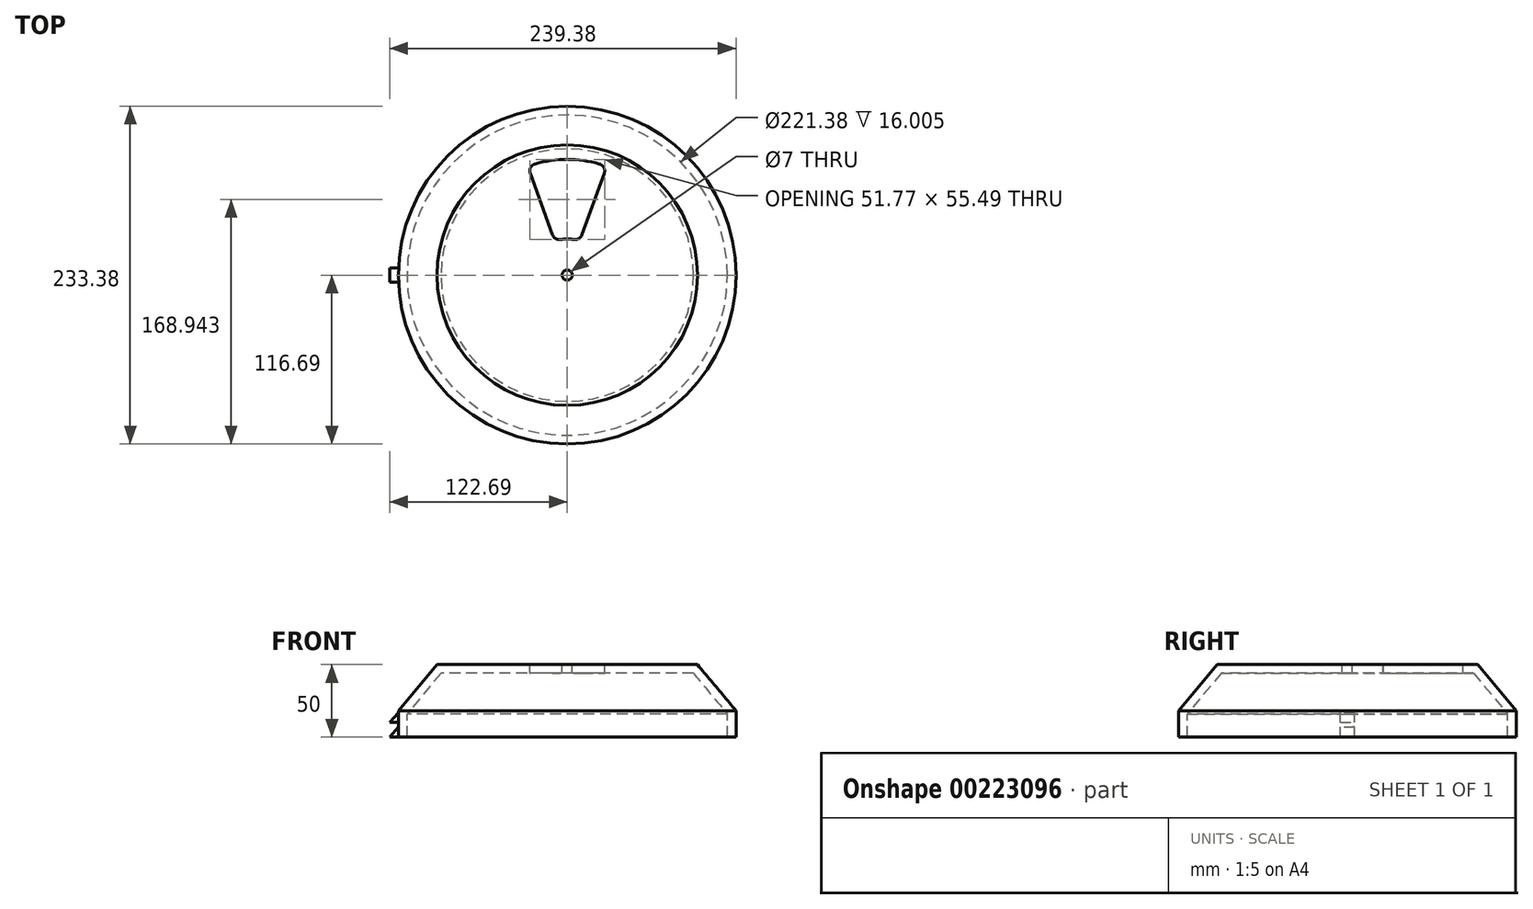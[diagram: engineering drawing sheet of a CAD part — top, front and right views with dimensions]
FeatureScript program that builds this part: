
annotation { "Feature Type Name" : "Feature", "Feature Type Description" : "" }
export const myFeature = defineFeature(function(context is Context, id is Id, definition is map)
    precondition{}
    {
        {
            var Q0;
            Q0=qCreatedBy(makeId("Front.planeOp"),FACE);
            var sketch = newSketch(context, id + "F0", { "sketchPlane" : qUnion([Q0])});
            skLineSegment(sketch, "E0", {"start": v(0, 0) * mm, "end": v(90, 0) * mm});
            skLineSegment(sketch, "E1", {"start": v(0, 0) * mm, "end": v(0, -6) * mm});
            skLineSegment(sketch, "E2", {"start": v(0, -6) * mm, "end": v(87.2, -6) * mm});
            skLineSegment(sketch, "E3", {"start": v(110.7, -34) * mm, "end": v(116.7, -31.81) * mm, "construction": true});
            skLineSegment(sketch, "E4", {"start": v(110.7, -34) * mm, "end": v(110.7, -50) * mm});
            skLineSegment(sketch, "E5", {"start": v(110.7, -50) * mm, "end": v(116.7, -50) * mm});
            skLineSegment(sketch, "E6", {"start": v(116.7, -50) * mm, "end": v(116.7, -31.81) * mm});
            skLineSegment(sketch, "E7", {"start": v(110.7, -34) * mm, "end": v(87.2, -6) * mm});
            skLineSegment(sketch, "E8", {"start": v(90, 0) * mm, "end": v(116.7, -31.81) * mm});
            skLineSegment(sketch, "E9", {"start": v(90, 0) * mm, "end": v(107.7, 0) * mm, "construction": true});
            skSolve(sketch);
        }
        {
            var Q0;
            Q0=makeQuery(id+"F0.imprint","IMPRINT",FACE,{"disambiguationData":[TD([[makeQuery(id+"F0.imprint","IMPRINT",EDGE,{"derivedFrom":sQuery(id+"F0.wireOp",EDGE,"E0")}),-1.0]])]});
            var Q1;
            Q1=sQuery(id+"F0.wireOp",EDGE,"E1");
            revolve(context, id + "F1", {"entities" : qUnion([Q0]), "axis" : qUnion([Q1]), "revolveType" : RevolveType.FULL});
        }
        {
            var Q0;
            Q0=makeQuery(id+"F1.opRevolve","SWEPT_FACE",FACE,{"disambiguationData":[OSD([sQuery(id+"F0.wireOp",EDGE,"E0")])]});
            var sketch = newSketch(context, id + "F2", { "sketchPlane" : qUnion([Q0])});
            skCircle(sketch, "E10", {"center": v(0, 0) * mm, "radius": 3.5 * mm});
            skSolve(sketch);
        }
        {
            var Q0;
            Q0 = qSketchRegion(id + "F2", true);
            extrude(context, id + "F3", {"entities" : qUnion([Q0]), "operationType" : NewBodyOperationType.REMOVE, "oppositeDirection" : true, "depth" : 25 * mm});
        }
        {
            var Q0;
            Q0=makeQuery(id+"F1.opRevolve","SWEPT_FACE",FACE,{"disambiguationData":[OSD([sQuery(id+"F0.wireOp",EDGE,"E0")])]});
            var sketch = newSketch(context, id + "F4", { "sketchPlane" : qUnion([Q0])});
            skLineSegment(sketch, "E11", {"start": v(0, 0) * mm, "end": v(0, 76.23) * mm, "construction": true});
            skLineSegment(sketch, "E12", {"start": v(0, 0) * mm, "end": v(-8.55, 23.5) * mm, "construction": true});
            skLineSegment(sketch, "E13", {"start": v(-8.55, 23.5) * mm, "end": v(-27.36, 75.18) * mm});
            skArc(sketch, "E14", {"start": v(0, 25) * mm, "mid": v(-4.34, 24.62) * mm, "end": v(-8.55, 23.5) * mm});
            skArc(sketch, "E15", {"start": v(0, 80) * mm, "mid": v(-13.9, 78.78) * mm, "end": v(-27.36, 75.18) * mm});
            skArc(sketch, "E16.MirrorCS", {"start": v(0, 80) * mm, "mid": v(13.9, 78.78) * mm, "end": v(27.36, 75.18) * mm});
            skLineSegment(sketch, "E17.MirrorCS", {"start": v(8.55, 23.5) * mm, "end": v(27.36, 75.18) * mm});
            skArc(sketch, "E18.MirrorCS", {"start": v(0, 25) * mm, "mid": v(4.34, 24.62) * mm, "end": v(8.55, 23.5) * mm});
            skSolve(sketch);
        }
        {
            var Q0;
            Q0 = qSketchRegion(id + "F4", true);
            extrude(context, id + "F5", {"entities" : qUnion([Q0]), "operationType" : NewBodyOperationType.REMOVE, "oppositeDirection" : true, "depth" : 25 * mm});
        }
        {
            var Q0;
            Q0=makeQuery(id+"F5.boolean.opBoolean","COPY",EDGE,{"derivedFrom":makeQuery(id+"F5.opExtrude","SWEPT_EDGE",EDGE,{"disambiguationData":[OSD([sQuery(id+"F4.wireOp",EDGE,"E17.MirrorCS"),sQuery(id+"F4.wireOp",EDGE,"E18.MirrorCS")])]})});
            var Q1;
            Q1=makeQuery(id+"F5.boolean.opBoolean","COPY",EDGE,{"derivedFrom":makeQuery(id+"F5.opExtrude","SWEPT_EDGE",EDGE,{"disambiguationData":[OSD([sQuery(id+"F4.wireOp",EDGE,"E13"),sQuery(id+"F4.wireOp",EDGE,"E14")])]})});
            var Q2;
            Q2=makeQuery(id+"F5.boolean.opBoolean","COPY",EDGE,{"derivedFrom":makeQuery(id+"F5.opExtrude","SWEPT_EDGE",EDGE,{"disambiguationData":[OSD([sQuery(id+"F0.wireOp",EDGE,"E0"),sQuery(id+"F0.wireOp",EDGE,"IK25yoJP-COcX-T8gp-FXQI-EpYJyZZEoqKl"),sQuery(id+"F4.wireOp",EDGE,"E16.MirrorCS"),sQuery(id+"F4.wireOp",EDGE,"E17.MirrorCS")])]})});
            var Q3;
            Q3=makeQuery(id+"F5.boolean.opBoolean","COPY",EDGE,{"derivedFrom":makeQuery(id+"F5.opExtrude","SWEPT_EDGE",EDGE,{"disambiguationData":[OSD([sQuery(id+"F0.wireOp",EDGE,"E0"),sQuery(id+"F0.wireOp",EDGE,"IK25yoJP-COcX-T8gp-FXQI-EpYJyZZEoqKl"),sQuery(id+"F4.wireOp",EDGE,"E13"),sQuery(id+"F4.wireOp",EDGE,"E15")])]})});
            fillet(context, id + "F6", {"entities" : qUnion([Q0, Q1, Q2, Q3]), "radius" : 5 * mm, "tangentPropagation" : true, "allowEdgeOverflow" : false});
        }
        {
            var Q0;
            Q0=qCreatedBy(makeId("Front.planeOp"),FACE);
            var sketch = newSketch(context, id + "F7", { "sketchPlane" : qUnion([Q0])});
            skLineSegment(sketch, "E19.0", {"start": v(-114.7, -50) * mm, "end": v(116.7, -50) * mm, "construction": true});
            skLineSegment(sketch, "E20", {"start": v(-114.7, -50) * mm, "end": v(-122.7, -50) * mm});
            skLineSegment(sketch, "E21", {"start": v(-122.7, -50) * mm, "end": v(-114.7, -41) * mm});
            skLineSegment(sketch, "E22", {"start": v(-114.7, -41) * mm, "end": v(-114.7, -50) * mm});
            skLineSegment(sketch, "E23", {"start": v(-114.7, -40) * mm, "end": v(-122.7, -40) * mm});
            skLineSegment(sketch, "E24", {"start": v(-122.7, -40) * mm, "end": v(-114.7, -31) * mm});
            skLineSegment(sketch, "E25", {"start": v(-114.7, -31) * mm, "end": v(-114.7, -40) * mm});
            skLineSegment(sketch, "E26", {"start": v(-116.7, -50) * mm, "end": v(-116.7, -30) * mm, "construction": true});
            skSolve(sketch);
        }
        {
            var Q0;
            Q0 = qSketchRegion(id + "F7", true);
            extrude(context, id + "F8", {"entities" : qUnion([Q0]), "operationType" : NewBodyOperationType.ADD, "endBound" : BoundingType.SYMMETRIC, "depth" : 10 * mm});
        }
    });
